# Revit family: DTM15N.1.24
name_source: partatom
category: Luminarias
units: mm (PartAtom-declared; Revit-internal decimal feet)

## family parameters
Compartido = No
Corte con vacíos al cargar = No
Cota de conector redondo = Diámetro de uso
Origen de luz = Sí
Punto de cálculo de habitación = No
Se basa en plano de trabajo = Sí
Siempre vertical = Sí
Tipo de pieza = Normal

## types (3) — shared parameters
Cambio de temperatura de color de luz atenuada = <Ninguno>
Comentarios de vataje = 90-277V
Elevación por defecto = 1219 mm
Fabricante = BRILLANT
Filtro de color = 16777215
Lámpara = CITIZEN
Watt per fixture = 13.8
Ángulo de inclinación = 60.00°

## per-type parameters (varying)
| type | Archivo de red fotométrica | Descripción | Modelo |
| SPOT RIEL_DTM15U.1.24 | generic | LUMINARIA DIRIGIBLE TIPO PUNTUAL DE UN CABEZAL COMPATIBLE CON RIEL DE 6 ENTRADAS Y 3 CIRCUITOS, CUERPO DE ALUMINIO ACABADO EN COLOR NEGRO, IP 20, PESO 0.84Kg, TIPO DE LED CITIZEN CON 13.8W TOTAL, 1024 LUMENES, 74LM/W, IRC 90, TEMPERATURA EN BLANCO CALIDO 2700K, 50 MIL HORAS DE VIDA PROMEDIO, APERTURA DE 24 GRADOS EN STOCK, ALIMENTADO A 90-277V/50-60Hz | DTM15U.1.24 |
| SPOT RIEL_DTM15U.1.16 | generic | LUMINARIA DIRIGIBLE TIPO PUNTUAL DE UN CABEZAL COMPATIBLE CON RIEL DE 6 ENTRADAS Y 3 CIRCUITOS, CUERPO DE ALUMINIO ACABADO EN COLOR NEGRO, IP 20, PESO 0.84Kg, TIPO DE LED CITIZEN CON 13.8W TOTAL, 1024 LUMENES, 74LM/W, IRC 90, TEMPERATURA EN BLANCO CALIDO 2700K, 50 MIL HORAS DE VIDA PROMEDIO, APERTURA DE 16 GRADOS POR PROYECTO, ALIMENTADO A 90-277V/50-60Hz | DTM15U.1.16 |
| SPOT RIEL_DTM15N.1.24 | TL36-15W-840-B-24_IESNA95.IES | LUMINARIA DIRIGIBLE TIPO PUNTUAL DE UN CABEZAL COMPATIBLE CON RIEL DE 6 ENTRADAS Y 3 CIRCUITOS, CUERPO DE ALUMINIO ACABADO EN COLOR NEGRO, IP 20, PESO 0.84Kg, TIPO DE LED CITIZEN CON 13.8W TOTAL, 1024 LUMENES, 74LM/W, IRC 90, TEMPERATURA EN BLANCO FRIO 4000K, 50 MIL HORAS DE VIDA PROMEDIO, APERTURA DE 24 GRADOS EN STOCK, ALIMENTADO A 90-277V/50-60Hz | DTM15N.1.24 |

## geometry (parser evidence)
native form markers: Blend x2
no freeform markers — native parametric forms only
